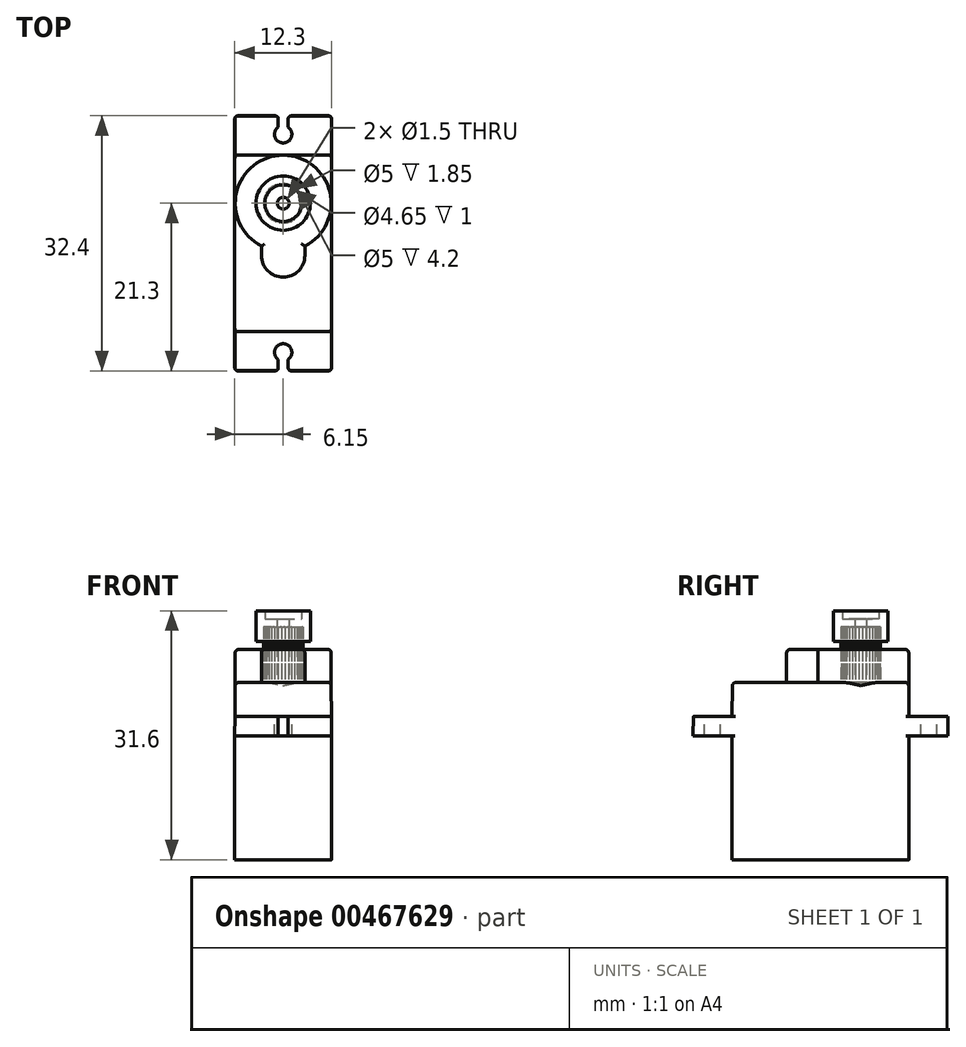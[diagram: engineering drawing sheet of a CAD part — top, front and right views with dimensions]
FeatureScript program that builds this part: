
annotation { "Feature Type Name" : "Feature", "Feature Type Description" : "" }
export const myFeature = defineFeature(function(context is Context, id is Id, definition is map)
    precondition{}
    {
        {
            var Q0;
            Q0=qCreatedBy(makeId("Top.planeOp"),FACE);
            var sketch = newSketch(context, id + "F0", { "sketchPlane" : qUnion([Q0])});
            skLineSegment(sketch, "E0.bottom", {"start": v(6.15, -11.25) * mm, "end": v(-6.15, -11.25) * mm});
            skLineSegment(sketch, "E0.top", {"start": v(6.15, 11.25) * mm, "end": v(-6.15, 11.25) * mm});
            skLineSegment(sketch, "E0.left", {"start": v(6.15, -11.25) * mm, "end": v(6.15, 11.25) * mm});
            skLineSegment(sketch, "E0.right", {"start": v(-6.15, -11.25) * mm, "end": v(-6.15, 11.25) * mm});
            skPoint(sketch, "E0.middle", {"position": v(0, 0) * mm});
            skSolve(sketch);
        }
        {
            var Q0;
            Q0=qSketchRegion(id+"F0",true);
            extrude(context, id + "F1", {"entities" : qUnion([Q0]), "depth" : (22.5 - 15.7) * mm, "hasDraft" : true, "draftAngle" : .5 * degree, "draftPullDirection" : true, "hasSecondDirection" : true, "secondDirectionOppositeDirection" : true, "secondDirectionDepth" : 15.7 * mm});
        }
        {
            var Q0;
            Q0=qCreatedBy(makeId("Top.planeOp"),FACE);
            var sketch = newSketch(context, id + "F2", { "sketchPlane" : qUnion([Q0])});
            skLineSegment(sketch, "E1.bottom", {"start": v(6.15, -16.2) * mm, "end": v(-6.15, -16.2) * mm});
            skLineSegment(sketch, "E1.top", {"start": v(6.15, 16.2) * mm, "end": v(-6.15, 16.2) * mm});
            skLineSegment(sketch, "E1.left", {"start": v(6.15, -16.2) * mm, "end": v(6.15, 16.2) * mm});
            skLineSegment(sketch, "E1.right", {"start": v(-6.15, -16.2) * mm, "end": v(-6.15, 16.2) * mm});
            skPoint(sketch, "E1.middle", {"position": v(0, 0) * mm});
            skSolve(sketch);
        }
        {
            var Q0;
            Q0=qSketchRegion(id+"F2",true);
            extrude(context, id + "F3", {"entities" : qUnion([Q0]), "operationType" : NewBodyOperationType.ADD, "depth" : 2.5 * mm, "hasDraft" : true, "draftAngle" : .5 * degree, "draftPullDirection" : true});
        }
        {
            var Q0;
            {var subQ0=sQuery(id+"F2.wireOp",EDGE,"E1.top");var subQ1=sQuery(id+"F2.wireOp",EDGE,"E1.right");var subQ2=sQuery(id+"F2.wireOp",EDGE,"E1.left");Q0=makeQuery(id+"F3.boolean.opBoolean","SPLIT",FACE,{"disambiguationData":[TD([makeQuery(id+"F1.opExtrude","SWEPT_FACE",FACE,{"disambiguationData":[OSD([sQuery(id+"F0.wireOp",EDGE,"E0.top")])]})])],"derivedFrom":makeQuery(id+"F3.opExtrude","CAP_FACE",FACE,{"disambiguationData":[OSD([sQuery(id+"F2.wireOp",EDGE,"E1.bottom"),subQ0,subQ2,subQ1])],"isStart":false})});}
            var sketch = newSketch(context, id + "F4", { "sketchPlane" : qUnion([Q0])});
            skArc(sketch, "E2", {"start": v(-0.63, 14.76) * mm, "mid": v(0, 12.75) * mm, "end": v(0.63, 14.76) * mm});
            skLineSegment(sketch, "E3", {"start": v(0, 0) * mm, "end": v(0, 13.85) * mm, "construction": true});
            skLineSegment(sketch, "E4", {"start": v(-0.63, 14.76) * mm, "end": v(-0.63, 16.2) * mm});
            skLineSegment(sketch, "E5", {"start": v(-0.62, 16.2) * mm, "end": v(0.62, 16.2) * mm});
            skLineSegment(sketch, "E6", {"start": v(0.62, 16.2) * mm, "end": v(0.62, 14.76) * mm});
            skLineSegment(sketch, "E7", {"start": v(0, 13.85) * mm, "end": v(0, 16.2) * mm, "construction": true});
            skLineSegment(sketch, "E8.MirrorCS", {"start": v(0.62, -16.2) * mm, "end": v(0.62, -14.76) * mm});
            skLineSegment(sketch, "E9.MirrorCS", {"start": v(-0.62, -16.2) * mm, "end": v(0.62, -16.2) * mm});
            skLineSegment(sketch, "E10.MirrorCS", {"start": v(-0.63, -14.76) * mm, "end": v(-0.63, -16.2) * mm});
            skArc(sketch, "E11.MirrorCS", {"start": v(-0.63, -14.76) * mm, "mid": v(0, -12.75) * mm, "end": v(0.63, -14.76) * mm});
            skSolve(sketch);
        }
        {
            var Q0;
            Q0=qSketchRegion(id+"F4",true);
            extrude(context, id + "F5", {"entities" : qUnion([Q0]), "operationType" : NewBodyOperationType.REMOVE, "endBound" : BoundingType.THROUGH_ALL, "oppositeDirection" : true, "depth" : 25 * mm});
        }
        {
            var Q0;
            Q0=makeQuery(id+"F1.*.split.splitOp","SPLIT",EDGE,{"derivedFrom":makeQuery(id+"F1.opExtrude","SWEPT_EDGE",EDGE,{"disambiguationData":[OSD([sQuery(id+"F0.wireOp",EDGE,"E0.bottom"),sQuery(id+"F0.wireOp",EDGE,"E0.left")])]})});
            var Q1;
            Q1=makeQuery(id+"F1.*.split.splitOp","SPLIT",EDGE,{"derivedFrom":makeQuery(id+"F1.opExtrude","SWEPT_EDGE",EDGE,{"disambiguationData":[OSD([sQuery(id+"F0.wireOp",EDGE,"E0.bottom"),sQuery(id+"F0.wireOp",EDGE,"E0.left")])]}),"isFromBackBody":true});
            var Q2;
            Q2=makeQuery(id+"F1.*.split.splitOp","SPLIT",EDGE,{"derivedFrom":makeQuery(id+"F1.opExtrude","SWEPT_EDGE",EDGE,{"disambiguationData":[OSD([sQuery(id+"F0.wireOp",EDGE,"E0.bottom"),sQuery(id+"F0.wireOp",EDGE,"E0.right")])]}),"isFromBackBody":true});
            var Q3;
            Q3=makeQuery(id+"F1.*.split.splitOp","SPLIT",EDGE,{"derivedFrom":makeQuery(id+"F1.opExtrude","SWEPT_EDGE",EDGE,{"disambiguationData":[OSD([sQuery(id+"F0.wireOp",EDGE,"E0.bottom"),sQuery(id+"F0.wireOp",EDGE,"E0.right")])]})});
            var Q4;
            Q4=makeQuery(id+"F1.opExtrude","CAP_FACE",FACE,{"disambiguationData":[OSD([sQuery(id+"F0.wireOp",EDGE,"E0.bottom"),sQuery(id+"F0.wireOp",EDGE,"E0.top"),sQuery(id+"F0.wireOp",EDGE,"E0.left"),sQuery(id+"F0.wireOp",EDGE,"E0.right")])],"isStart":false});
            var Q5;
            Q5=makeQuery(id+"F1.*.split.splitOp","SPLIT",EDGE,{"derivedFrom":makeQuery(id+"F1.opExtrude","SWEPT_EDGE",EDGE,{"disambiguationData":[OSD([sQuery(id+"F0.wireOp",EDGE,"E0.top"),sQuery(id+"F0.wireOp",EDGE,"E0.right")])]})});
            var Q6;
            Q6=makeQuery(id+"F1.*.split.splitOp","SPLIT",EDGE,{"derivedFrom":makeQuery(id+"F1.opExtrude","SWEPT_EDGE",EDGE,{"disambiguationData":[OSD([sQuery(id+"F0.wireOp",EDGE,"E0.top"),sQuery(id+"F0.wireOp",EDGE,"E0.right")])]}),"isFromBackBody":true});
            var Q7;
            Q7=makeQuery(id+"F1.*.split.splitOp","SPLIT",EDGE,{"derivedFrom":makeQuery(id+"F1.opExtrude","SWEPT_EDGE",EDGE,{"disambiguationData":[OSD([sQuery(id+"F0.wireOp",EDGE,"E0.top"),sQuery(id+"F0.wireOp",EDGE,"E0.left")])]}),"isFromBackBody":true});
            var Q8;
            Q8=makeQuery(id+"F1.*.split.splitOp","SPLIT",EDGE,{"derivedFrom":makeQuery(id+"F1.opExtrude","SWEPT_EDGE",EDGE,{"disambiguationData":[OSD([sQuery(id+"F0.wireOp",EDGE,"E0.top"),sQuery(id+"F0.wireOp",EDGE,"E0.left")])]})});
            var Q9;
            Q9=makeQuery(id+"F3.opExtrude","SWEPT_EDGE",EDGE,{"disambiguationData":[OSD([sQuery(id+"F2.wireOp",EDGE,"E1.top"),sQuery(id+"F2.wireOp",EDGE,"E1.left")])]});
            var Q10;
            Q10=makeQuery(id+"F5.boolean.opBoolean","INTERSECT",EDGE,{"derivedFrom":[makeQuery(id+"F3.opExtrude","SWEPT_FACE",FACE,{"disambiguationData":[OSD([sQuery(id+"F2.wireOp",EDGE,"E1.top")])]}),makeQuery(id+"F5.opExtrude","SWEPT_FACE",FACE,{"disambiguationData":[OSD([sQuery(id+"F4.wireOp",EDGE,"E6")])]})]});
            var Q11;
            Q11=makeQuery(id+"F5.boolean.opBoolean","INTERSECT",EDGE,{"derivedFrom":[makeQuery(id+"F3.opExtrude","SWEPT_FACE",FACE,{"disambiguationData":[OSD([sQuery(id+"F2.wireOp",EDGE,"E1.top")])]}),makeQuery(id+"F5.opExtrude","SWEPT_FACE",FACE,{"disambiguationData":[OSD([sQuery(id+"F4.wireOp",EDGE,"E4")])]})]});
            var Q12;
            Q12=makeQuery(id+"F3.opExtrude","SWEPT_EDGE",EDGE,{"disambiguationData":[OSD([sQuery(id+"F2.wireOp",EDGE,"E1.top"),sQuery(id+"F2.wireOp",EDGE,"E1.right")])]});
            var Q13;
            Q13=makeQuery(id+"F3.opExtrude","SWEPT_EDGE",EDGE,{"disambiguationData":[OSD([sQuery(id+"F2.wireOp",EDGE,"E1.bottom"),sQuery(id+"F2.wireOp",EDGE,"E1.right")])]});
            var Q14;
            Q14=makeQuery(id+"F5.boolean.opBoolean","INTERSECT",EDGE,{"derivedFrom":[makeQuery(id+"F3.opExtrude","SWEPT_FACE",FACE,{"disambiguationData":[OSD([sQuery(id+"F2.wireOp",EDGE,"E1.bottom")])]}),makeQuery(id+"F5.opExtrude","SWEPT_FACE",FACE,{"disambiguationData":[OSD([sQuery(id+"F4.wireOp",EDGE,"E10.MirrorCS")])]})]});
            var Q15;
            Q15=makeQuery(id+"F5.boolean.opBoolean","INTERSECT",EDGE,{"derivedFrom":[makeQuery(id+"F3.opExtrude","SWEPT_FACE",FACE,{"disambiguationData":[OSD([sQuery(id+"F2.wireOp",EDGE,"E1.bottom")])]}),makeQuery(id+"F5.opExtrude","SWEPT_FACE",FACE,{"disambiguationData":[OSD([sQuery(id+"F4.wireOp",EDGE,"E8.MirrorCS")])]})]});
            var Q16;
            Q16=makeQuery(id+"F3.opExtrude","SWEPT_EDGE",EDGE,{"disambiguationData":[OSD([sQuery(id+"F2.wireOp",EDGE,"E1.bottom"),sQuery(id+"F2.wireOp",EDGE,"E1.left")])]});
            fillet(context, id + "F6", {"entities" : qUnion([Q0, Q1, Q2, Q3, Q4, Q5, Q6, Q7, Q8, Q9, Q10, Q11, Q12, Q13, Q14, Q15, Q16]), "radius" : .4 * mm, "tangentPropagation" : true, "allowEdgeOverflow" : false});
        }
        {
            var Q0;
            Q0=makeQuery(id+"F1.opExtrude","CAP_FACE",FACE,{"disambiguationData":[OSD([sQuery(id+"F0.wireOp",EDGE,"E0.bottom"),sQuery(id+"F0.wireOp",EDGE,"E0.top"),sQuery(id+"F0.wireOp",EDGE,"E0.left"),sQuery(id+"F0.wireOp",EDGE,"E0.right")])],"isStart":false});
            var sketch = newSketch(context, id + "F7", { "sketchPlane" : qUnion([Q0])});
            skArc(sketch, "E12", {"start": v(2.75, -0.34) * mm, "mid": v(0, 11.2) * mm, "end": v(-2.75, -0.34) * mm});
            skLineSegment(sketch, "E13", {"start": v(-2.75, -0.34) * mm, "end": v(-2.75, -1.56) * mm});
            skLineSegment(sketch, "E14", {"start": v(2.75, -0.34) * mm, "end": v(2.75, -1.56) * mm});
            skArc(sketch, "E15", {"start": v(-2.75, -1.56) * mm, "mid": v(0, -4.3) * mm, "end": v(2.75, -1.56) * mm});
            skCircle(sketch, "E16", {"center": v(0, 5.1) * mm, "radius": 2.5 * mm});
            skSolve(sketch);
        }
        {
            var Q0;
            Q0=qSketchRegion(id+"F7",true);
            extrude(context, id + "F8", {"entities" : qUnion([Q0]), "operationType" : NewBodyOperationType.ADD, "depth" : 4.2 * mm, "hasSecondDirection" : true, "secondDirectionBound" : SecondDirectionBoundingType.UP_TO_NEXT, "secondDirectionOppositeDirection" : true, "secondDirectionDepth" : 25 * mm});
        }
        {
            var Q0;
            Q0=makeQuery(id+"F8.opExtrude","CAP_EDGE",EDGE,{"disambiguationData":[OSD([sQuery(id+"F7.wireOp",EDGE,"E12")])],"isStart":false});
            var Q1;
            Q1=makeQuery(id+"F8.opExtrude","CAP_EDGE",EDGE,{"disambiguationData":[OSD([sQuery(id+"F7.wireOp",EDGE,"E14")])],"isStart":false});
            var Q2;
            Q2=makeQuery(id+"F8.opExtrude","CAP_EDGE",EDGE,{"disambiguationData":[OSD([sQuery(id+"F7.wireOp",EDGE,"E15")])],"isStart":false});
            var Q3;
            Q3=makeQuery(id+"F8.opExtrude","CAP_EDGE",EDGE,{"disambiguationData":[OSD([sQuery(id+"F7.wireOp",EDGE,"E13")])],"isStart":false});
            fillet(context, id + "F9", {"entities" : qUnion([Q0, Q1, Q2, Q3]), "radius" : .4 * mm, "tangentPropagation" : true, "allowEdgeOverflow" : false});
        }
        {
            var Q0;
            Q0=makeQuery(id+"F8.opExtrude","CAP_FACE",FACE,{"disambiguationData":[OSD([sQuery(id+"F7.wireOp",EDGE,"E12"),sQuery(id+"F7.wireOp",EDGE,"E13"),sQuery(id+"F7.wireOp",EDGE,"E14"),sQuery(id+"F7.wireOp",EDGE,"E15"),sQuery(id+"F7.wireOp",EDGE,"E16")])],"isStart":false});
            var sketch = newSketch(context, id + "F10", { "sketchPlane" : qUnion([Q0])});
            skCircle(sketch, "E17", {"center": v(0, 5.1) * mm, "radius": 2.3 * mm, "construction": true});
            skLineSegment(sketch, "E18", {"start": v(-0.23, 7.39) * mm, "end": v(-0.06, 7.57) * mm});
            skLineSegment(sketch, "E19", {"start": v(0.23, 7.39) * mm, "end": v(0.06, 7.57) * mm});
            skArc(sketch, "E20", {"start": v(0.06, 7.57) * mm, "mid": v(0, 7.6) * mm, "end": v(-0.06, 7.57) * mm});
            skLineSegment(sketch, "E21", {"start": v(-0.23, 7.39) * mm, "end": v(0, 5.1) * mm, "construction": true});
            skLineSegment(sketch, "E22", {"start": v(0.23, 7.39) * mm, "end": v(0, 5.1) * mm, "construction": true});
            skLineSegment(sketch, "E23.1.0", {"start": v(-0.67, 7.3) * mm, "end": v(-0.54, 7.51) * mm});
            skArc(sketch, "E23.1.1", {"start": v(-0.42, 7.54) * mm, "mid": v(-0.49, 7.55) * mm, "end": v(-0.54, 7.51) * mm});
            skLineSegment(sketch, "E23.1.2", {"start": v(-0.23, 7.39) * mm, "end": v(-0.42, 7.54) * mm});
            skLineSegment(sketch, "E23.2.0", {"start": v(-1.08, 7.13) * mm, "end": v(-1, 7.36) * mm});
            skArc(sketch, "E23.2.1", {"start": v(-0.9, 7.4) * mm, "mid": v(-0.96, 7.4) * mm, "end": v(-1, 7.36) * mm});
            skLineSegment(sketch, "E23.2.2", {"start": v(-0.67, 7.3) * mm, "end": v(-0.9, 7.4) * mm});
            skLineSegment(sketch, "E23.3.0", {"start": v(-1.46, 6.88) * mm, "end": v(-1.42, 7.12) * mm});
            skArc(sketch, "E23.3.1", {"start": v(-1.32, 7.19) * mm, "mid": v(-1.39, 7.18) * mm, "end": v(-1.42, 7.12) * mm});
            skLineSegment(sketch, "E23.3.2", {"start": v(-1.08, 7.13) * mm, "end": v(-1.32, 7.19) * mm});
            skLineSegment(sketch, "E23.4.0", {"start": v(-1.78, 6.56) * mm, "end": v(-1.8, 6.8) * mm});
            skArc(sketch, "E23.4.1", {"start": v(-1.7, 6.9) * mm, "mid": v(-1.77, 6.87) * mm, "end": v(-1.8, 6.8) * mm});
            skLineSegment(sketch, "E23.4.2", {"start": v(-1.46, 6.88) * mm, "end": v(-1.7, 6.9) * mm});
            skLineSegment(sketch, "E23.5.0", {"start": v(-2.03, 6.18) * mm, "end": v(-2.09, 6.42) * mm});
            skArc(sketch, "E23.5.1", {"start": v(-2.02, 6.52) * mm, "mid": v(-2.08, 6.49) * mm, "end": v(-2.09, 6.42) * mm});
            skLineSegment(sketch, "E23.5.2", {"start": v(-1.78, 6.56) * mm, "end": v(-2.02, 6.52) * mm});
            skLineSegment(sketch, "E23.6.0", {"start": v(-2.2, 5.77) * mm, "end": v(-2.3, 6) * mm});
            skArc(sketch, "E23.6.1", {"start": v(-2.26, 6.1) * mm, "mid": v(-2.3, 6.06) * mm, "end": v(-2.3, 6) * mm});
            skLineSegment(sketch, "E23.6.2", {"start": v(-2.03, 6.18) * mm, "end": v(-2.26, 6.1) * mm});
            skLineSegment(sketch, "E23.7.0", {"start": v(-2.29, 5.33) * mm, "end": v(-2.44, 5.52) * mm});
            skArc(sketch, "E23.7.1", {"start": v(-2.41, 5.64) * mm, "mid": v(-2.45, 5.59) * mm, "end": v(-2.44, 5.52) * mm});
            skLineSegment(sketch, "E23.7.2", {"start": v(-2.2, 5.77) * mm, "end": v(-2.41, 5.64) * mm});
            skLineSegment(sketch, "E23.8.0", {"start": v(-2.29, 4.87) * mm, "end": v(-2.47, 5.04) * mm});
            skArc(sketch, "E23.8.1", {"start": v(-2.47, 5.16) * mm, "mid": v(-2.5, 5.1) * mm, "end": v(-2.47, 5.04) * mm});
            skLineSegment(sketch, "E23.8.2", {"start": v(-2.29, 5.33) * mm, "end": v(-2.47, 5.16) * mm});
            skLineSegment(sketch, "E23.9.0", {"start": v(-2.2, 4.43) * mm, "end": v(-2.41, 4.56) * mm});
            skArc(sketch, "E23.9.1", {"start": v(-2.44, 4.68) * mm, "mid": v(-2.45, 4.61) * mm, "end": v(-2.41, 4.56) * mm});
            skLineSegment(sketch, "E23.9.2", {"start": v(-2.29, 4.87) * mm, "end": v(-2.44, 4.68) * mm});
            skLineSegment(sketch, "E23.10.0", {"start": v(-2.03, 4.02) * mm, "end": v(-2.26, 4.1) * mm});
            skArc(sketch, "E23.10.1", {"start": v(-2.3, 4.2) * mm, "mid": v(-2.3, 4.14) * mm, "end": v(-2.26, 4.1) * mm});
            skLineSegment(sketch, "E23.10.2", {"start": v(-2.2, 4.43) * mm, "end": v(-2.3, 4.2) * mm});
            skLineSegment(sketch, "E23.11.0", {"start": v(-1.78, 3.64) * mm, "end": v(-2.02, 3.68) * mm});
            skArc(sketch, "E23.11.1", {"start": v(-2.09, 3.78) * mm, "mid": v(-2.08, 3.71) * mm, "end": v(-2.02, 3.68) * mm});
            skLineSegment(sketch, "E23.11.2", {"start": v(-2.03, 4.02) * mm, "end": v(-2.09, 3.78) * mm});
            skLineSegment(sketch, "E23.12.0", {"start": v(-1.46, 3.32) * mm, "end": v(-1.7, 3.3) * mm});
            skArc(sketch, "E23.12.1", {"start": v(-1.8, 3.4) * mm, "mid": v(-1.77, 3.33) * mm, "end": v(-1.7, 3.3) * mm});
            skLineSegment(sketch, "E23.12.2", {"start": v(-1.78, 3.64) * mm, "end": v(-1.8, 3.4) * mm});
            skLineSegment(sketch, "E23.13.0", {"start": v(-1.08, 3.07) * mm, "end": v(-1.32, 3.01) * mm});
            skArc(sketch, "E23.13.1", {"start": v(-1.42, 3.08) * mm, "mid": v(-1.39, 3.02) * mm, "end": v(-1.32, 3.01) * mm});
            skLineSegment(sketch, "E23.13.2", {"start": v(-1.46, 3.32) * mm, "end": v(-1.42, 3.08) * mm});
            skLineSegment(sketch, "E23.14.0", {"start": v(-0.67, 2.9) * mm, "end": v(-0.9, 2.8) * mm});
            skArc(sketch, "E23.14.1", {"start": v(-1, 2.84) * mm, "mid": v(-0.96, 2.8) * mm, "end": v(-0.9, 2.8) * mm});
            skLineSegment(sketch, "E23.14.2", {"start": v(-1.08, 3.07) * mm, "end": v(-1, 2.84) * mm});
            skLineSegment(sketch, "E23.15.0", {"start": v(-0.23, 2.81) * mm, "end": v(-0.42, 2.66) * mm});
            skArc(sketch, "E23.15.1", {"start": v(-0.54, 2.69) * mm, "mid": v(-0.49, 2.65) * mm, "end": v(-0.42, 2.66) * mm});
            skLineSegment(sketch, "E23.15.2", {"start": v(-0.67, 2.9) * mm, "end": v(-0.54, 2.69) * mm});
            skLineSegment(sketch, "E23.16.0", {"start": v(0.23, 2.81) * mm, "end": v(0.06, 2.63) * mm});
            skArc(sketch, "E23.16.1", {"start": v(-0.06, 2.63) * mm, "mid": v(0, 2.6) * mm, "end": v(0.06, 2.63) * mm});
            skLineSegment(sketch, "E23.16.2", {"start": v(-0.23, 2.81) * mm, "end": v(-0.06, 2.63) * mm});
            skLineSegment(sketch, "E23.17.0", {"start": v(0.67, 2.9) * mm, "end": v(0.54, 2.69) * mm});
            skArc(sketch, "E23.17.1", {"start": v(0.42, 2.66) * mm, "mid": v(0.49, 2.65) * mm, "end": v(0.54, 2.69) * mm});
            skLineSegment(sketch, "E23.17.2", {"start": v(0.23, 2.81) * mm, "end": v(0.42, 2.66) * mm});
            skLineSegment(sketch, "E23.18.0", {"start": v(1.08, 3.07) * mm, "end": v(1, 2.84) * mm});
            skArc(sketch, "E23.18.1", {"start": v(0.9, 2.8) * mm, "mid": v(0.96, 2.8) * mm, "end": v(1, 2.84) * mm});
            skLineSegment(sketch, "E23.18.2", {"start": v(0.67, 2.9) * mm, "end": v(0.9, 2.8) * mm});
            skLineSegment(sketch, "E23.19.0", {"start": v(1.46, 3.32) * mm, "end": v(1.42, 3.08) * mm});
            skArc(sketch, "E23.19.1", {"start": v(1.32, 3.01) * mm, "mid": v(1.39, 3.02) * mm, "end": v(1.42, 3.08) * mm});
            skLineSegment(sketch, "E23.19.2", {"start": v(1.08, 3.07) * mm, "end": v(1.32, 3.01) * mm});
            skLineSegment(sketch, "E23.20.0", {"start": v(1.78, 3.64) * mm, "end": v(1.8, 3.4) * mm});
            skArc(sketch, "E23.20.1", {"start": v(1.7, 3.3) * mm, "mid": v(1.77, 3.33) * mm, "end": v(1.8, 3.4) * mm});
            skLineSegment(sketch, "E23.20.2", {"start": v(1.46, 3.32) * mm, "end": v(1.7, 3.3) * mm});
            skLineSegment(sketch, "E23.21.0", {"start": v(2.03, 4.02) * mm, "end": v(2.09, 3.78) * mm});
            skArc(sketch, "E23.21.1", {"start": v(2.02, 3.68) * mm, "mid": v(2.08, 3.71) * mm, "end": v(2.09, 3.78) * mm});
            skLineSegment(sketch, "E23.21.2", {"start": v(1.78, 3.64) * mm, "end": v(2.02, 3.68) * mm});
            skLineSegment(sketch, "E23.22.0", {"start": v(2.2, 4.43) * mm, "end": v(2.3, 4.2) * mm});
            skArc(sketch, "E23.22.1", {"start": v(2.26, 4.1) * mm, "mid": v(2.3, 4.14) * mm, "end": v(2.3, 4.2) * mm});
            skLineSegment(sketch, "E23.22.2", {"start": v(2.03, 4.02) * mm, "end": v(2.26, 4.1) * mm});
            skLineSegment(sketch, "E23.23.0", {"start": v(2.29, 4.87) * mm, "end": v(2.44, 4.68) * mm});
            skArc(sketch, "E23.23.1", {"start": v(2.41, 4.56) * mm, "mid": v(2.45, 4.61) * mm, "end": v(2.44, 4.68) * mm});
            skLineSegment(sketch, "E23.23.2", {"start": v(2.2, 4.43) * mm, "end": v(2.41, 4.56) * mm});
            skLineSegment(sketch, "E23.24.0", {"start": v(2.29, 5.33) * mm, "end": v(2.47, 5.16) * mm});
            skArc(sketch, "E23.24.1", {"start": v(2.47, 5.04) * mm, "mid": v(2.5, 5.1) * mm, "end": v(2.47, 5.16) * mm});
            skLineSegment(sketch, "E23.24.2", {"start": v(2.29, 4.87) * mm, "end": v(2.47, 5.04) * mm});
            skLineSegment(sketch, "E23.25.0", {"start": v(2.2, 5.77) * mm, "end": v(2.41, 5.64) * mm});
            skArc(sketch, "E23.25.1", {"start": v(2.44, 5.52) * mm, "mid": v(2.45, 5.59) * mm, "end": v(2.41, 5.64) * mm});
            skLineSegment(sketch, "E23.25.2", {"start": v(2.29, 5.33) * mm, "end": v(2.44, 5.52) * mm});
            skLineSegment(sketch, "E23.26.0", {"start": v(2.03, 6.18) * mm, "end": v(2.26, 6.1) * mm});
            skArc(sketch, "E23.26.1", {"start": v(2.3, 6) * mm, "mid": v(2.3, 6.06) * mm, "end": v(2.26, 6.1) * mm});
            skLineSegment(sketch, "E23.26.2", {"start": v(2.2, 5.77) * mm, "end": v(2.3, 6) * mm});
            skLineSegment(sketch, "E23.27.0", {"start": v(1.78, 6.56) * mm, "end": v(2.02, 6.52) * mm});
            skArc(sketch, "E23.27.1", {"start": v(2.09, 6.42) * mm, "mid": v(2.08, 6.49) * mm, "end": v(2.02, 6.52) * mm});
            skLineSegment(sketch, "E23.27.2", {"start": v(2.03, 6.18) * mm, "end": v(2.09, 6.42) * mm});
            skLineSegment(sketch, "E23.28.0", {"start": v(1.46, 6.88) * mm, "end": v(1.7, 6.9) * mm});
            skArc(sketch, "E23.28.1", {"start": v(1.8, 6.8) * mm, "mid": v(1.77, 6.87) * mm, "end": v(1.7, 6.9) * mm});
            skLineSegment(sketch, "E23.28.2", {"start": v(1.78, 6.56) * mm, "end": v(1.8, 6.8) * mm});
            skLineSegment(sketch, "E23.29.0", {"start": v(1.08, 7.13) * mm, "end": v(1.32, 7.19) * mm});
            skArc(sketch, "E23.29.1", {"start": v(1.42, 7.12) * mm, "mid": v(1.39, 7.18) * mm, "end": v(1.32, 7.19) * mm});
            skLineSegment(sketch, "E23.29.2", {"start": v(1.46, 6.88) * mm, "end": v(1.42, 7.12) * mm});
            skLineSegment(sketch, "E23.30.0", {"start": v(0.67, 7.3) * mm, "end": v(0.9, 7.4) * mm});
            skArc(sketch, "E23.30.1", {"start": v(1, 7.36) * mm, "mid": v(0.96, 7.4) * mm, "end": v(0.9, 7.4) * mm});
            skLineSegment(sketch, "E23.30.2", {"start": v(1.08, 7.13) * mm, "end": v(1, 7.36) * mm});
            skLineSegment(sketch, "E23.31.0", {"start": v(0.23, 7.39) * mm, "end": v(0.42, 7.54) * mm});
            skArc(sketch, "E23.31.1", {"start": v(0.54, 7.51) * mm, "mid": v(0.49, 7.55) * mm, "end": v(0.42, 7.54) * mm});
            skLineSegment(sketch, "E23.31.2", {"start": v(0.67, 7.3) * mm, "end": v(0.54, 7.51) * mm});
            skCircle(sketch, "E24", {"center": v(0, 5.1) * mm, "radius": 0.75 * mm});
            skSolve(sketch);
        }
        {
            var Q0;
            Q0=qSketchRegion(id+"F10",true);
            extrude(context, id + "F11", {"entities" : qUnion([Q0]), "depth" : 2.85 * mm, "hasSecondDirection" : true, "secondDirectionBound" : SecondDirectionBoundingType.UP_TO_NEXT, "secondDirectionOppositeDirection" : true, "secondDirectionDepth" : 25 * mm});
        }
        {
            var Q0;
            Q0=qCreatedBy(makeId("Right.planeOp"),FACE);
            var sketch = newSketch(context, id + "F12", { "sketchPlane" : qUnion([Q0])});
            skLineSegment(sketch, "E25.0", {"start": v(4.35, 13.85) * mm, "end": v(5.85, 13.85) * mm, "construction": true});
            skLineSegment(sketch, "E26", {"start": v(5.85, 13.85) * mm, "end": v(7.6, 13.85) * mm});
            skLineSegment(sketch, "E27", {"start": v(7.6, 13.85) * mm, "end": v(7.6, 12) * mm});
            skLineSegment(sketch, "E28", {"start": v(7.6, 12) * mm, "end": v(8.55, 12) * mm});
            skLineSegment(sketch, "E29", {"start": v(8.55, 12) * mm, "end": v(8.55, 15.9) * mm});
            skLineSegment(sketch, "E30", {"start": v(8.55, 15.9) * mm, "end": v(7.43, 15.9) * mm});
            skLineSegment(sketch, "E31", {"start": v(7.43, 15.9) * mm, "end": v(7.43, 14.9) * mm});
            skLineSegment(sketch, "E32", {"start": v(7.43, 14.9) * mm, "end": v(5.85, 14.9) * mm});
            skLineSegment(sketch, "E33", {"start": v(5.85, 14.9) * mm, "end": v(5.85, 13.85) * mm});
            skLineSegment(sketch, "E34", {"start": v(5.1, 13.85) * mm, "end": v(5.1, 16.3) * mm, "construction": true});
            skLineSegment(sketch, "E35.0", {"start": v(2.6, 11) * mm, "end": v(7.6, 11) * mm, "construction": true});
            skSolve(sketch);
        }
        {
            var Q0;
            Q0=qSketchRegion(id+"F12",true);
            var Q1;
            Q1=sQuery(id+"F12.wireOp",EDGE,"E34");
            revolve(context, id + "F13", {"entities" : qUnion([Q0]), "axis" : qUnion([Q1]), "revolveType" : RevolveType.FULL});
        }
    });
